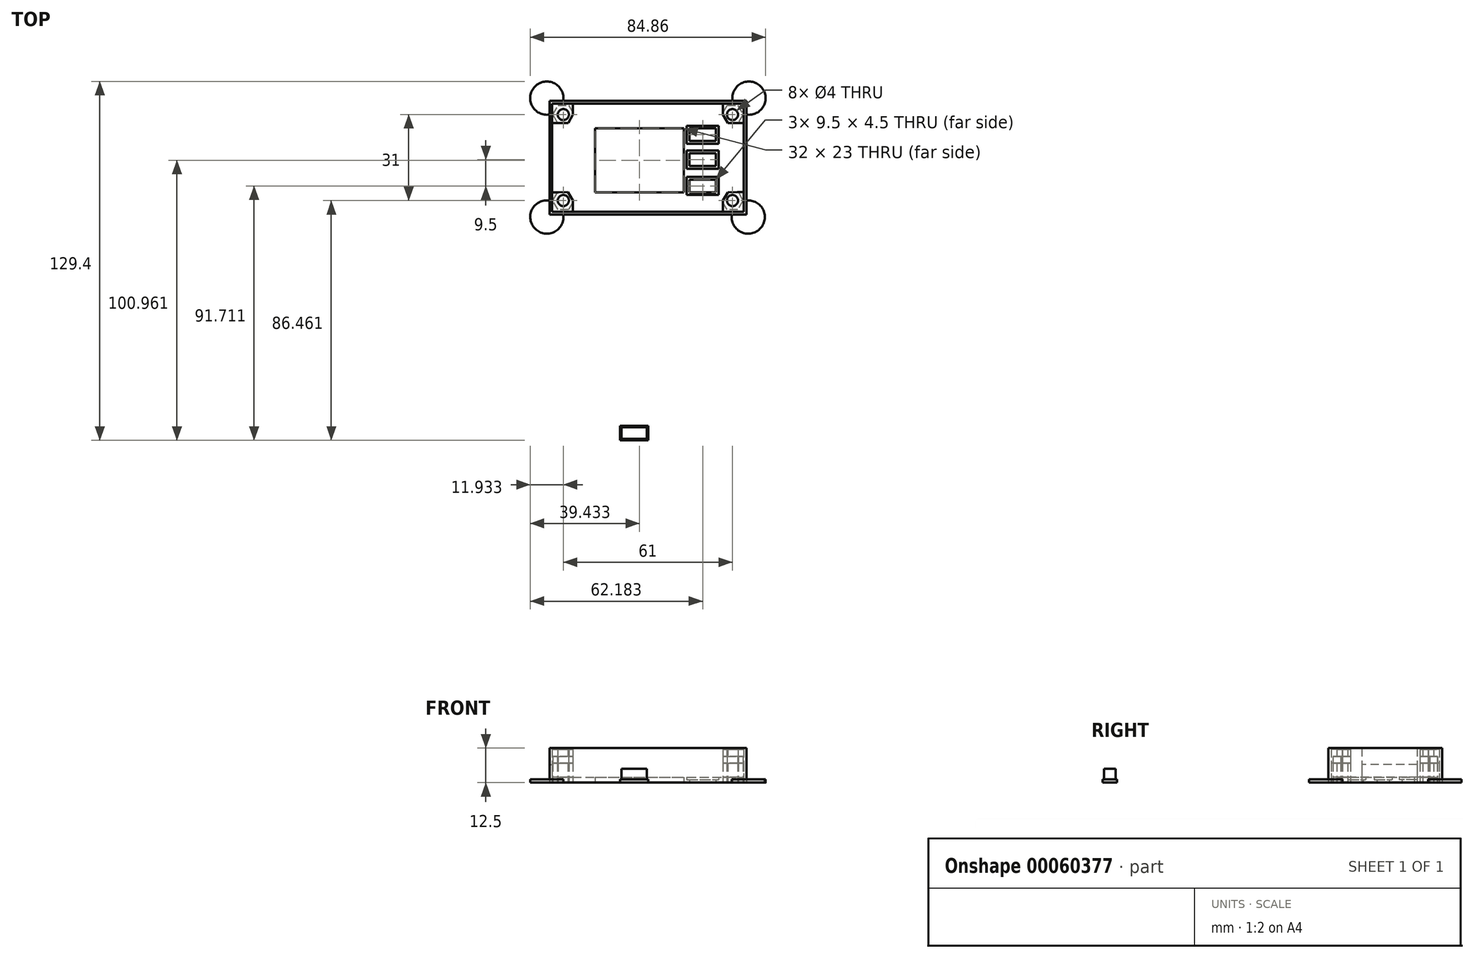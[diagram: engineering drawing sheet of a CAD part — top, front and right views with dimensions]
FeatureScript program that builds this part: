
annotation { "Feature Type Name" : "Feature", "Feature Type Description" : "" }
export const myFeature = defineFeature(function(context is Context, id is Id, definition is map)
    precondition{}
    {
        {
            var Q0;
            Q0=qCreatedBy(makeId("Top.planeOp"),FACE);
            var sketch = newSketch(context, id + "F0", { "sketchPlane" : qUnion([Q0])});
            skCircle(sketch, "E0.cCircle", {"center": v(0, 0) * mm, "radius": 3 * mm, "construction": true});
            skLineSegment(sketch, "E0.0", {"start": v(1.73, 3) * mm, "end": v(3.46, 0) * mm});
            skLineSegment(sketch, "E0.1", {"start": v(3.46, 0) * mm, "end": v(1.74, -3) * mm});
            skLineSegment(sketch, "E0.2", {"start": v(1.74, -3) * mm, "end": v(-1.73, -3) * mm});
            skLineSegment(sketch, "E0.3", {"start": v(-1.73, -3) * mm, "end": v(-3.46, 0) * mm});
            skLineSegment(sketch, "E0.4", {"start": v(-3.46, 0) * mm, "end": v(-1.74, 3) * mm});
            skLineSegment(sketch, "E0.5", {"start": v(-1.74, 3) * mm, "end": v(1.73, 3) * mm});
            skPoint(sketch, "E0.0.midPoint", {"position": v(2.6, 1.5) * mm});
            skCircle(sketch, "E1", {"center": v(0, 0) * mm, "radius": 1.5 * mm});
            skLineSegment(sketch, "E2.bottom", {"start": v(-12.76, 68.41) * mm, "end": v(56.24, 68.41) * mm});
            skLineSegment(sketch, "E2.top", {"start": v(-12.76, 29.41) * mm, "end": v(56.24, 29.41) * mm});
            skLineSegment(sketch, "E2.left", {"start": v(-12.76, 68.41) * mm, "end": v(-12.76, 29.41) * mm});
            skLineSegment(sketch, "E2.right", {"start": v(56.24, 68.41) * mm, "end": v(56.24, 29.41) * mm});
            skPoint(sketch, "E3.0.midPoint", {"position": v(-6.16, 65.92) * mm});
            skLineSegment(sketch, "E3.3", {"start": v(-10.48, 61.4) * mm, "end": v(-12.22, 64.4) * mm, "construction": true});
            skLineSegment(sketch, "E3.2", {"start": v(-7.02, 61.41) * mm, "end": v(-10.48, 61.4) * mm});
            skLineSegment(sketch, "E3.1", {"start": v(-5.3, 64.42) * mm, "end": v(-7.02, 61.41) * mm});
            skLineSegment(sketch, "E3.0", {"start": v(-7.03, 67.41) * mm, "end": v(-5.3, 64.42) * mm, "construction": true});
            skLineSegment(sketch, "E3.4", {"start": v(-12.22, 64.4) * mm, "end": v(-10.5, 67.4) * mm, "construction": true});
            skLineSegment(sketch, "E3.5", {"start": v(-10.5, 67.4) * mm, "end": v(-7.03, 67.41) * mm, "construction": true});
            skCircle(sketch, "E4", {"center": v(-8.76, 64.41) * mm, "radius": 1.5 * mm, "construction": true});
            skCircle(sketch, "E3.cCircle", {"center": v(-8.76, 64.41) * mm, "radius": 3 * mm, "construction": true});
            skPoint(sketch, "E5.0.midPoint", {"position": v(-6.16, 34.92) * mm});
            skLineSegment(sketch, "E5.3", {"start": v(-10.48, 30.4) * mm, "end": v(-12.22, 33.4) * mm, "construction": true});
            skLineSegment(sketch, "E5.2", {"start": v(-7.02, 30.41) * mm, "end": v(-10.48, 30.4) * mm, "construction": true});
            skLineSegment(sketch, "E5.1", {"start": v(-5.3, 33.42) * mm, "end": v(-7.02, 30.41) * mm, "construction": true});
            skLineSegment(sketch, "E5.0", {"start": v(-7.03, 36.41) * mm, "end": v(-5.3, 33.42) * mm});
            skLineSegment(sketch, "E5.4", {"start": v(-12.22, 33.4) * mm, "end": v(-10.5, 36.4) * mm, "construction": true});
            skLineSegment(sketch, "E5.5", {"start": v(-10.5, 36.4) * mm, "end": v(-7.03, 36.41) * mm});
            skCircle(sketch, "E6", {"center": v(-8.76, 33.41) * mm, "radius": 1.5 * mm, "construction": true});
            skCircle(sketch, "E5.cCircle", {"center": v(-8.76, 33.41) * mm, "radius": 3 * mm, "construction": true});
            skPoint(sketch, "E7.0.midPoint", {"position": v(54.84, 65.92) * mm});
            skLineSegment(sketch, "E7.3", {"start": v(50.52, 61.4) * mm, "end": v(48.78, 64.4) * mm});
            skLineSegment(sketch, "E7.2", {"start": v(53.98, 61.41) * mm, "end": v(50.52, 61.4) * mm});
            skLineSegment(sketch, "E7.1", {"start": v(55.7, 64.42) * mm, "end": v(53.98, 61.41) * mm, "construction": true});
            skLineSegment(sketch, "E7.0", {"start": v(53.97, 67.41) * mm, "end": v(55.7, 64.42) * mm, "construction": true});
            skLineSegment(sketch, "E7.4", {"start": v(48.78, 64.4) * mm, "end": v(50.5, 67.4) * mm, "construction": true});
            skLineSegment(sketch, "E7.5", {"start": v(50.5, 67.4) * mm, "end": v(53.97, 67.41) * mm, "construction": true});
            skCircle(sketch, "E8", {"center": v(52.24, 64.41) * mm, "radius": 1.5 * mm, "construction": true});
            skCircle(sketch, "E7.cCircle", {"center": v(52.24, 64.41) * mm, "radius": 3 * mm, "construction": true});
            skPoint(sketch, "E9.0.midPoint", {"position": v(54.84, 34.92) * mm});
            skLineSegment(sketch, "E9.3", {"start": v(50.52, 30.4) * mm, "end": v(48.78, 33.4) * mm, "construction": true});
            skLineSegment(sketch, "E9.2", {"start": v(53.98, 30.41) * mm, "end": v(50.52, 30.4) * mm, "construction": true});
            skLineSegment(sketch, "E9.1", {"start": v(55.7, 33.42) * mm, "end": v(53.98, 30.41) * mm, "construction": true});
            skLineSegment(sketch, "E9.0", {"start": v(53.97, 36.41) * mm, "end": v(55.7, 33.42) * mm, "construction": true});
            skLineSegment(sketch, "E9.4", {"start": v(48.78, 33.4) * mm, "end": v(50.5, 36.4) * mm});
            skLineSegment(sketch, "E9.5", {"start": v(50.5, 36.4) * mm, "end": v(53.97, 36.41) * mm});
            skCircle(sketch, "E10", {"center": v(52.24, 33.41) * mm, "radius": 1.5 * mm, "construction": true});
            skCircle(sketch, "E9.cCircle", {"center": v(52.24, 33.41) * mm, "radius": 3 * mm, "construction": true});
            skLineSegment(sketch, "E11", {"start": v(48.78, 33.4) * mm, "end": v(48.78, 29.41) * mm});
            skLineSegment(sketch, "E12", {"start": v(53.97, 36.41) * mm, "end": v(56.24, 36.41) * mm});
            skCircle(sketch, "E13.0", {"center": v(52.24, 33.41) * mm, "radius": 2 * mm});
            skLineSegment(sketch, "E14.0", {"start": v(50.34, 30.1) * mm, "end": v(48.52, 33.25) * mm});
            skLineSegment(sketch, "E14.1", {"start": v(54.15, 30.11) * mm, "end": v(50.34, 30.1) * mm});
            skLineSegment(sketch, "E14.2", {"start": v(56.05, 33.42) * mm, "end": v(54.15, 30.11) * mm});
            skLineSegment(sketch, "E14.3", {"start": v(54.23, 36.56) * mm, "end": v(56.05, 33.42) * mm});
            skLineSegment(sketch, "E15", {"start": v(-5.3, 33.42) * mm, "end": v(-5.3, 29.41) * mm});
            skLineSegment(sketch, "E16", {"start": v(-10.5, 36.4) * mm, "end": v(-12.76, 36.4) * mm});
            skLineSegment(sketch, "E17", {"start": v(-10.48, 61.4) * mm, "end": v(-12.76, 61.4) * mm});
            skLineSegment(sketch, "E18", {"start": v(-5.3, 64.42) * mm, "end": v(-5.3, 68.41) * mm});
            skLineSegment(sketch, "E19", {"start": v(53.98, 61.41) * mm, "end": v(56.24, 61.42) * mm});
            skLineSegment(sketch, "E20", {"start": v(48.78, 64.4) * mm, "end": v(48.78, 68.41) * mm});
            skCircle(sketch, "E21.0", {"center": v(52.24, 64.41) * mm, "radius": 2 * mm});
            skCircle(sketch, "E22.0", {"center": v(-8.76, 64.41) * mm, "radius": 2 * mm});
            skCircle(sketch, "E23.0", {"center": v(-8.76, 33.41) * mm, "radius": 2 * mm});
            skLineSegment(sketch, "E24.0", {"start": v(-6.86, 67.71) * mm, "end": v(-5.03, 64.57) * mm});
            skLineSegment(sketch, "E24.1", {"start": v(-10.67, 67.7) * mm, "end": v(-6.86, 67.71) * mm});
            skLineSegment(sketch, "E24.2", {"start": v(-12.57, 64.4) * mm, "end": v(-10.67, 67.7) * mm});
            skLineSegment(sketch, "E24.3", {"start": v(-10.74, 61.26) * mm, "end": v(-12.57, 64.4) * mm});
            skLineSegment(sketch, "E25.0", {"start": v(-12.57, 33.4) * mm, "end": v(-10.76, 36.56) * mm});
            skLineSegment(sketch, "E25.1", {"start": v(-10.66, 30.1) * mm, "end": v(-12.57, 33.4) * mm});
            skLineSegment(sketch, "E25.2", {"start": v(-6.85, 30.11) * mm, "end": v(-10.66, 30.1) * mm});
            skLineSegment(sketch, "E25.3", {"start": v(-5.03, 33.27) * mm, "end": v(-6.85, 30.11) * mm});
            skLineSegment(sketch, "E26.0", {"start": v(56.05, 64.42) * mm, "end": v(50.35, 54.5) * mm});
            skLineSegment(sketch, "E26.1", {"start": v(54.14, 67.71) * mm, "end": v(56.05, 64.42) * mm});
            skLineSegment(sketch, "E26.2", {"start": v(50.33, 67.7) * mm, "end": v(54.14, 67.71) * mm});
            skLineSegment(sketch, "E26.3", {"start": v(48.52, 64.55) * mm, "end": v(50.33, 67.7) * mm});
            skPoint(sketch, "E27", {"position": v(2.74, 36.41) * mm});
            skLineSegment(sketch, "E28.bottom", {"start": v(2.74, 36.41) * mm, "end": v(34.74, 36.41) * mm});
            skLineSegment(sketch, "E28.top", {"start": v(2.74, 59.41) * mm, "end": v(34.74, 59.41) * mm});
            skLineSegment(sketch, "E28.left", {"start": v(2.74, 36.41) * mm, "end": v(2.74, 59.41) * mm});
            skLineSegment(sketch, "E28.right", {"start": v(34.74, 36.41) * mm, "end": v(34.74, 59.41) * mm});
            skPoint(sketch, "E29", {"position": v(36.74, 59.41) * mm});
            skLineSegment(sketch, "E30.bottom", {"start": v(36.74, 59.41) * mm, "end": v(46.24, 59.41) * mm});
            skLineSegment(sketch, "E30.top", {"start": v(36.74, 54.91) * mm, "end": v(46.24, 54.91) * mm});
            skLineSegment(sketch, "E30.left", {"start": v(36.74, 59.41) * mm, "end": v(36.74, 54.91) * mm});
            skLineSegment(sketch, "E30.right", {"start": v(46.24, 59.41) * mm, "end": v(46.24, 54.91) * mm});
            skLineSegment(sketch, "E31.bottom", {"start": v(36.74, 36.41) * mm, "end": v(46.24, 36.41) * mm});
            skLineSegment(sketch, "E31.top", {"start": v(36.74, 40.91) * mm, "end": v(46.24, 40.91) * mm});
            skLineSegment(sketch, "E31.left", {"start": v(36.74, 36.41) * mm, "end": v(36.74, 40.91) * mm});
            skLineSegment(sketch, "E31.right", {"start": v(46.24, 36.41) * mm, "end": v(46.24, 40.91) * mm});
            skLineSegment(sketch, "E32.bottom", {"start": v(36.74, 45.91) * mm, "end": v(46.24, 45.91) * mm});
            skLineSegment(sketch, "E32.top", {"start": v(36.74, 50.41) * mm, "end": v(46.24, 50.41) * mm});
            skLineSegment(sketch, "E32.left", {"start": v(36.74, 45.91) * mm, "end": v(36.74, 50.41) * mm});
            skLineSegment(sketch, "E32.right", {"start": v(46.24, 45.91) * mm, "end": v(46.24, 50.41) * mm});
            skLineSegment(sketch, "E33.0", {"start": v(-13.76, 69.41) * mm, "end": v(-13.76, 28.41) * mm});
            skLineSegment(sketch, "E33.1", {"start": v(-13.76, 69.41) * mm, "end": v(57.24, 69.41) * mm});
            skLineSegment(sketch, "E33.2", {"start": v(57.24, 69.41) * mm, "end": v(57.24, 28.41) * mm});
            skLineSegment(sketch, "E33.3", {"start": v(-13.76, 28.41) * mm, "end": v(57.24, 28.41) * mm});
            skPoint(sketch, "E34", {"position": v(-13.76, 60.41) * mm});
            skPoint(sketch, "E35", {"position": v(-13.76, 40.41) * mm});
            skLineSegment(sketch, "E36", {"start": v(-13.76, 60.41) * mm, "end": v(-12.76, 60.41) * mm});
            skLineSegment(sketch, "E37", {"start": v(-13.76, 40.41) * mm, "end": v(-12.76, 40.41) * mm});
            skLineSegment(sketch, "E38.bottom", {"start": v(13.09, -34.33) * mm, "end": v(22.29, -34.33) * mm});
            skLineSegment(sketch, "E38.top", {"start": v(13.09, -38.53) * mm, "end": v(22.29, -38.53) * mm});
            skLineSegment(sketch, "E38.left", {"start": v(13.09, -34.33) * mm, "end": v(13.09, -38.53) * mm});
            skLineSegment(sketch, "E38.right", {"start": v(22.29, -34.33) * mm, "end": v(22.29, -38.53) * mm});
            skLineSegment(sketch, "E39.0", {"start": v(12.09, -33.33) * mm, "end": v(23.29, -33.33) * mm});
            skLineSegment(sketch, "E39.1", {"start": v(12.09, -33.33) * mm, "end": v(12.09, -39.53) * mm});
            skLineSegment(sketch, "E39.2", {"start": v(12.09, -39.53) * mm, "end": v(23.29, -39.53) * mm});
            skLineSegment(sketch, "E39.3", {"start": v(23.29, -33.33) * mm, "end": v(23.29, -39.53) * mm});
            skLineSegment(sketch, "E40.bottom", {"start": v(12.2, -48.35) * mm, "end": v(21.4, -48.35) * mm});
            skLineSegment(sketch, "E40.top", {"start": v(12.2, -52.55) * mm, "end": v(21.4, -52.55) * mm});
            skLineSegment(sketch, "E40.left", {"start": v(12.2, -48.35) * mm, "end": v(12.2, -52.55) * mm});
            skLineSegment(sketch, "E40.right", {"start": v(21.4, -48.35) * mm, "end": v(21.4, -52.55) * mm});
            skLineSegment(sketch, "E41.0", {"start": v(11.7, -47.85) * mm, "end": v(21.9, -47.85) * mm});
            skLineSegment(sketch, "E41.1", {"start": v(11.7, -47.85) * mm, "end": v(11.7, -53.05) * mm});
            skLineSegment(sketch, "E41.2", {"start": v(11.7, -53.05) * mm, "end": v(21.9, -53.05) * mm});
            skLineSegment(sketch, "E41.3", {"start": v(21.9, -47.85) * mm, "end": v(21.9, -53.05) * mm});
            skArc(sketch, "E42", {"start": v(57.24, 64.42) * mm, "mid": v(62.4, 74.6) * mm, "end": v(52.24, 69.41) * mm});
            skArc(sketch, "E43", {"start": v(52.24, 29.41) * mm, "mid": v(61.67, 22.77) * mm, "end": v(57.24, 33.42) * mm});
            skArc(sketch, "E44", {"start": v(-13.76, 33.4) * mm, "mid": v(-18.92, 23.23) * mm, "end": v(-8.76, 28.41) * mm});
            skArc(sketch, "E45", {"start": v(-8.76, 69.41) * mm, "mid": v(-18.93, 74.57) * mm, "end": v(-13.76, 64.4) * mm});
            skLineSegment(sketch, "E46.0", {"start": v(35.74, 53.91) * mm, "end": v(47.24, 53.91) * mm});
            skLineSegment(sketch, "E46.1", {"start": v(35.74, 60.41) * mm, "end": v(35.74, 53.91) * mm});
            skLineSegment(sketch, "E46.2", {"start": v(35.74, 60.41) * mm, "end": v(47.24, 60.41) * mm});
            skLineSegment(sketch, "E46.3", {"start": v(47.24, 60.41) * mm, "end": v(47.24, 53.91) * mm});
            skLineSegment(sketch, "E47.0", {"start": v(35.74, 51.41) * mm, "end": v(47.24, 51.41) * mm});
            skLineSegment(sketch, "E47.1", {"start": v(35.74, 44.91) * mm, "end": v(35.74, 51.41) * mm});
            skLineSegment(sketch, "E47.2", {"start": v(35.74, 44.91) * mm, "end": v(47.24, 44.91) * mm});
            skLineSegment(sketch, "E47.3", {"start": v(47.24, 44.91) * mm, "end": v(47.24, 51.41) * mm});
            skLineSegment(sketch, "E48.0", {"start": v(35.74, 41.91) * mm, "end": v(47.24, 41.91) * mm});
            skLineSegment(sketch, "E48.1", {"start": v(35.74, 35.41) * mm, "end": v(35.74, 41.91) * mm});
            skLineSegment(sketch, "E48.2", {"start": v(35.74, 35.41) * mm, "end": v(47.24, 35.41) * mm});
            skLineSegment(sketch, "E48.3", {"start": v(47.24, 35.41) * mm, "end": v(47.24, 41.91) * mm});
            skSolve(sketch);
        }
        {
            var Q0;
            {var subQ12=sQuery(id+"F0.wireOp",EDGE,"E14.1");Q0=makeQuery(id+"F0.imprint","IMPRINT",FACE,{"disambiguationData":[TD([[makeQuery(id+"F0.imprint","IMPRINT",EDGE,{"derivedFrom":subQ12}),1.0]])]});}
            var Q1;
            {var subQ6=sQuery(id+"F0.wireOp",EDGE,"E9.4");Q1=makeQuery(id+"F0.imprint","IMPRINT",FACE,{"disambiguationData":[TD([[makeQuery(id+"F0.imprint","IMPRINT",EDGE,{"derivedFrom":subQ6}),-1.0]])]});}
            var Q2;
            {var subQ5=sQuery(id+"F0.wireOp",EDGE,"E25.1");Q2=makeQuery(id+"F0.imprint","IMPRINT",FACE,{"disambiguationData":[TD([[makeQuery(id+"F0.imprint","IMPRINT",EDGE,{"derivedFrom":subQ5}),1.0]])]});}
            var Q3;
            {var subQ5=sQuery(id+"F0.wireOp",EDGE,"E5.0");Q3=makeQuery(id+"F0.imprint","IMPRINT",FACE,{"disambiguationData":[TD([[makeQuery(id+"F0.imprint","IMPRINT",EDGE,{"derivedFrom":subQ5}),-1.0]])]});}
            var Q4;
            {var subQ11=sQuery(id+"F0.wireOp",EDGE,"E24.1");Q4=makeQuery(id+"F0.imprint","IMPRINT",FACE,{"disambiguationData":[TD([[makeQuery(id+"F0.imprint","IMPRINT",EDGE,{"derivedFrom":subQ11}),1.0]])]});}
            var Q5;
            {var subQ5=sQuery(id+"F0.wireOp",EDGE,"E3.2");Q5=makeQuery(id+"F0.imprint","IMPRINT",FACE,{"disambiguationData":[TD([[makeQuery(id+"F0.imprint","IMPRINT",EDGE,{"derivedFrom":subQ5}),-1.0]])]});}
            var Q6;
            {var subQ7=sQuery(id+"F0.wireOp",EDGE,"E26.1");Q6=makeQuery(id+"F0.imprint","IMPRINT",FACE,{"disambiguationData":[TD([[makeQuery(id+"F0.imprint","IMPRINT",EDGE,{"derivedFrom":subQ7}),1.0]])]});}
            var Q7;
            {var subQ1=sQuery(id+"F0.wireOp",EDGE,"E7.3");Q7=makeQuery(id+"F0.imprint","IMPRINT",FACE,{"disambiguationData":[TD([[makeQuery(id+"F0.imprint","IMPRINT",EDGE,{"derivedFrom":subQ1}),-1.0]])]});}
            extrude(context, id + "F1", {"entities" : qUnion([Q0, Q1, Q2, Q3, Q4, Q5, Q6, Q7]), "depth" : 7 * mm});
        }
        {
            var Q0;
            {var subQ12=sQuery(id+"F0.wireOp",EDGE,"E14.1");Q0=makeQuery(id+"F0.imprint","IMPRINT",FACE,{"disambiguationData":[TD([[makeQuery(id+"F0.imprint","IMPRINT",EDGE,{"derivedFrom":subQ12}),1.0]])]});}
            var Q1;
            {var subQ7=sQuery(id+"F0.wireOp",EDGE,"E26.1");Q1=makeQuery(id+"F0.imprint","IMPRINT",FACE,{"disambiguationData":[TD([[makeQuery(id+"F0.imprint","IMPRINT",EDGE,{"derivedFrom":subQ7}),1.0]])]});}
            var Q2;
            {var subQ11=sQuery(id+"F0.wireOp",EDGE,"E24.1");Q2=makeQuery(id+"F0.imprint","IMPRINT",FACE,{"disambiguationData":[TD([[makeQuery(id+"F0.imprint","IMPRINT",EDGE,{"derivedFrom":subQ11}),1.0]])]});}
            var Q3;
            {var subQ5=sQuery(id+"F0.wireOp",EDGE,"E25.1");Q3=makeQuery(id+"F0.imprint","IMPRINT",FACE,{"disambiguationData":[TD([[makeQuery(id+"F0.imprint","IMPRINT",EDGE,{"derivedFrom":subQ5}),1.0]])]});}
            extrude(context, id + "F2", {"entities" : qUnion([Q0, Q1, Q2, Q3]), "endBound" : BoundingType.UP_TO_NEXT, "depth" : 25 * mm});
        }
        {
            var Q0;
            Q0=makeQuery(id+"F2.opExtrude","CAP_FACE",FACE,{"disambiguationData":[OSD([sQuery(id+"F0.wireOp",EDGE,"E2.top"),sQuery(id+"F0.wireOp",EDGE,"E2.right"),sQuery(id+"F0.wireOp",EDGE,"E9.4"),sQuery(id+"F0.wireOp",EDGE,"E9.5"),sQuery(id+"F0.wireOp",EDGE,"E11"),sQuery(id+"F0.wireOp",EDGE,"E12"),sQuery(id+"F0.wireOp",EDGE,"E13.0")])],"isStart":false});
            var Q1;
            Q1=makeQuery(id+"F2.opExtrude","CAP_FACE",FACE,{"disambiguationData":[OSD([sQuery(id+"F0.wireOp",EDGE,"E2.top"),sQuery(id+"F0.wireOp",EDGE,"E2.left"),sQuery(id+"F0.wireOp",EDGE,"E5.0"),sQuery(id+"F0.wireOp",EDGE,"E5.5"),sQuery(id+"F0.wireOp",EDGE,"E15"),sQuery(id+"F0.wireOp",EDGE,"E16"),sQuery(id+"F0.wireOp",EDGE,"E23.0")])],"isStart":false});
            var Q2;
            Q2=makeQuery(id+"F2.opExtrude","CAP_FACE",FACE,{"disambiguationData":[OSD([sQuery(id+"F0.wireOp",EDGE,"E2.bottom"),sQuery(id+"F0.wireOp",EDGE,"E2.left"),sQuery(id+"F0.wireOp",EDGE,"E3.2"),sQuery(id+"F0.wireOp",EDGE,"E3.1"),sQuery(id+"F0.wireOp",EDGE,"E17"),sQuery(id+"F0.wireOp",EDGE,"E18"),sQuery(id+"F0.wireOp",EDGE,"E22.0")])],"isStart":false});
            var Q3;
            Q3=makeQuery(id+"F2.opExtrude","CAP_FACE",FACE,{"disambiguationData":[OSD([sQuery(id+"F0.wireOp",EDGE,"E2.bottom"),sQuery(id+"F0.wireOp",EDGE,"E2.right"),sQuery(id+"F0.wireOp",EDGE,"E7.3"),sQuery(id+"F0.wireOp",EDGE,"E7.2"),sQuery(id+"F0.wireOp",EDGE,"E19"),sQuery(id+"F0.wireOp",EDGE,"E20"),sQuery(id+"F0.wireOp",EDGE,"E21.0")])],"isStart":false});
            extrude(context, id + "F3", {"entities" : qUnion([Q0, Q1, Q2, Q3]), "depth" : 2.5 * mm});
        }
        {
            var Q0;
            Q0=makeQuery(id+"F1.opExtrude","CAP_FACE",FACE,{"disambiguationData":[OSD([sQuery(id+"F0.wireOp",EDGE,"E2.top"),sQuery(id+"F0.wireOp",EDGE,"E2.right"),sQuery(id+"F0.wireOp",EDGE,"E9.4"),sQuery(id+"F0.wireOp",EDGE,"E9.5"),sQuery(id+"F0.wireOp",EDGE,"E11"),sQuery(id+"F0.wireOp",EDGE,"E12"),sQuery(id+"F0.wireOp",EDGE,"E13.0")])],"isStart":false});
            var Q1;
            Q1=makeQuery(id+"F1.opExtrude","CAP_FACE",FACE,{"disambiguationData":[OSD([sQuery(id+"F0.wireOp",EDGE,"E2.top"),sQuery(id+"F0.wireOp",EDGE,"E2.left"),sQuery(id+"F0.wireOp",EDGE,"E5.0"),sQuery(id+"F0.wireOp",EDGE,"E5.5"),sQuery(id+"F0.wireOp",EDGE,"E15"),sQuery(id+"F0.wireOp",EDGE,"E16"),sQuery(id+"F0.wireOp",EDGE,"E23.0")])],"isStart":false});
            var Q2;
            Q2=makeQuery(id+"F1.opExtrude","CAP_FACE",FACE,{"disambiguationData":[OSD([sQuery(id+"F0.wireOp",EDGE,"E2.bottom"),sQuery(id+"F0.wireOp",EDGE,"E2.left"),sQuery(id+"F0.wireOp",EDGE,"E3.2"),sQuery(id+"F0.wireOp",EDGE,"E3.1"),sQuery(id+"F0.wireOp",EDGE,"E17"),sQuery(id+"F0.wireOp",EDGE,"E18"),sQuery(id+"F0.wireOp",EDGE,"E22.0")])],"isStart":false});
            var Q3;
            Q3=makeQuery(id+"F1.opExtrude","CAP_FACE",FACE,{"disambiguationData":[OSD([sQuery(id+"F0.wireOp",EDGE,"E2.bottom"),sQuery(id+"F0.wireOp",EDGE,"E2.right"),sQuery(id+"F0.wireOp",EDGE,"E7.3"),sQuery(id+"F0.wireOp",EDGE,"E7.2"),sQuery(id+"F0.wireOp",EDGE,"E19"),sQuery(id+"F0.wireOp",EDGE,"E20"),sQuery(id+"F0.wireOp",EDGE,"E21.0")])],"isStart":false});
            extrude(context, id + "F4", {"entities" : qUnion([Q0, Q1, Q2, Q3]), "operationType" : NewBodyOperationType.ADD, "depth" : 5 * mm, "hasSecondDirection" : true, "secondDirectionOppositeDirection" : false, "secondDirectionDepth" : 2.5 * mm});
        }
        {
            var Q0;
            {var subQ14=sQuery(id+"F0.wireOp",EDGE,"E3.2");Q0=makeQuery(id+"F0.imprint","IMPRINT",FACE,{"disambiguationData":[TD([[makeQuery(id+"F0.imprint","IMPRINT",EDGE,{"derivedFrom":subQ14}),1.0]])]});}
            var Q1;
            Q1=makeQuery(id+"F0.imprint","IMPRINT",FACE,{"disambiguationData":[TD([[makeQuery(id+"F0.imprint","IMPRINT",EDGE,{"derivedFrom":sQuery(id+"F0.wireOp",EDGE,"E22.0")}),1.0]])]});
            var Q2;
            Q2=makeQuery(id+"F0.imprint","IMPRINT",FACE,{"disambiguationData":[TD([[makeQuery(id+"F0.imprint","IMPRINT",EDGE,{"derivedFrom":sQuery(id+"F0.wireOp",EDGE,"E21.0")}),1.0]])]});
            var Q3;
            Q3=makeQuery(id+"F0.imprint","IMPRINT",FACE,{"disambiguationData":[TD([[makeQuery(id+"F0.imprint","IMPRINT",EDGE,{"derivedFrom":sQuery(id+"F0.wireOp",EDGE,"E13.0")}),1.0]])]});
            var Q4;
            Q4=makeQuery(id+"F0.imprint","IMPRINT",FACE,{"disambiguationData":[TD([[makeQuery(id+"F0.imprint","IMPRINT",EDGE,{"derivedFrom":sQuery(id+"F0.wireOp",EDGE,"E23.0")}),1.0]])]});
            extrude(context, id + "F5", {"entities" : qUnion([Q0, Q1, Q2, Q3, Q4]), "depth" : 2 * mm});
        }
        {
            var Q0;
            Q0=makeQuery(id+"F0.imprint","IMPRINT",FACE,{"disambiguationData":[TD([[makeQuery(id+"F0.imprint","IMPRINT",EDGE,{"derivedFrom":sQuery(id+"F0.wireOp",EDGE,"E30.bottom")}),1.0]])]});
            var Q1;
            Q1=makeQuery(id+"F0.imprint","IMPRINT",FACE,{"disambiguationData":[TD([[makeQuery(id+"F0.imprint","IMPRINT",EDGE,{"derivedFrom":sQuery(id+"F0.wireOp",EDGE,"E32.bottom")}),-1.0]])]});
            var Q2;
            Q2=makeQuery(id+"F0.imprint","IMPRINT",FACE,{"disambiguationData":[TD([[makeQuery(id+"F0.imprint","IMPRINT",EDGE,{"derivedFrom":sQuery(id+"F0.wireOp",EDGE,"E31.bottom")}),-1.0]])]});
            extrude(context, id + "F6", {"entities" : qUnion([Q0, Q1, Q2]), "operationType" : NewBodyOperationType.ADD, "depth" : 1 * mm});
        }
        {
            var Q0;
            {var subQ18=sQuery(id+"F0.wireOp",EDGE,"E33.1");Q0=makeQuery(id+"F0.imprint","IMPRINT",FACE,{"disambiguationData":[TD([[makeQuery(id+"F0.imprint","IMPRINT",EDGE,{"derivedFrom":subQ18}),-1.0]])]});}
            var Q1;
            {var subQ0=sQuery(id+"F0.wireOp",EDGE,"E37");Q1=makeQuery(id+"F0.imprint","IMPRINT",FACE,{"disambiguationData":[TD([[makeQuery(id+"F0.imprint","IMPRINT",EDGE,{"derivedFrom":subQ0}),-1.0]])]});}
            extrude(context, id + "F7", {"entities" : qUnion([Q0, Q1]), "depth" : 12.5 * mm});
        }
        {
            var Q0;
            {var subQ0=sQuery(id+"F0.wireOp",EDGE,"E36");Q0=makeQuery(id+"F0.imprint","IMPRINT",FACE,{"disambiguationData":[TD([[makeQuery(id+"F0.imprint","IMPRINT",EDGE,{"derivedFrom":subQ0}),-1.0]])]});}
            extrude(context, id + "F8", {"entities" : qUnion([Q0]), "depth" : 6.5 * mm});
        }
        {
            var Q0;
            Q0=makeQuery(id+"F0.imprint","IMPRINT",FACE,{"disambiguationData":[TD([[makeQuery(id+"F0.imprint","IMPRINT",EDGE,{"derivedFrom":sQuery(id+"F0.wireOp",EDGE,"E40.bottom")}),1.0]])]});
            extrude(context, id + "F9", {"entities" : qUnion([Q0]), "depth" : 1.2 * mm});
        }
        {
            var Q0;
            Q0=makeQuery(id+"F0.imprint","IMPRINT",FACE,{"disambiguationData":[TD([[makeQuery(id+"F0.imprint","IMPRINT",EDGE,{"derivedFrom":sQuery(id+"F0.wireOp",EDGE,"E40.bottom")}),-1.0]])]});
            extrude(context, id + "F10", {"entities" : qUnion([Q0]), "operationType" : NewBodyOperationType.ADD, "depth" : 5 * mm});
        }
        {
            var Q0;
            {var subQ3=sQuery(id+"F0.wireOp",EDGE,"E44");Q0=makeQuery(id+"F0.imprint","IMPRINT",FACE,{"disambiguationData":[TD([[makeQuery(id+"F0.imprint","IMPRINT",EDGE,{"derivedFrom":subQ3}),1.0]])]});}
            var Q1;
            {var subQ3=sQuery(id+"F0.wireOp",EDGE,"E45");Q1=makeQuery(id+"F0.imprint","IMPRINT",FACE,{"disambiguationData":[TD([[makeQuery(id+"F0.imprint","IMPRINT",EDGE,{"derivedFrom":subQ3}),1.0]])]});}
            var Q2;
            {var subQ3=sQuery(id+"F0.wireOp",EDGE,"E42");Q2=makeQuery(id+"F0.imprint","IMPRINT",FACE,{"disambiguationData":[TD([[makeQuery(id+"F0.imprint","IMPRINT",EDGE,{"derivedFrom":subQ3}),1.0]])]});}
            var Q3;
            {var subQ0=sQuery(id+"F0.wireOp",EDGE,"E33.3");var subQ1=sQuery(id+"F0.wireOp",EDGE,"E33.2");var subQ2=makeQuery(id+"F0.imprint","INTERSECT",VERTEX,{"derivedFrom":[subQ1,subQ0]});Q3=makeQuery(id+"F0.imprint","IMPRINT",FACE,{"disambiguationData":[TD([[makeQuery(id+"F0.imprint","IMPRINT",EDGE,{"disambiguationData":[TD([[subQ2,1.0]])],"derivedFrom":subQ1}),1.0]])]});}
            extrude(context, id + "F11", {"entities" : qUnion([Q0, Q1, Q2, Q3]), "operationType" : NewBodyOperationType.ADD, "depth" : 1.2 * mm});
        }
    });
